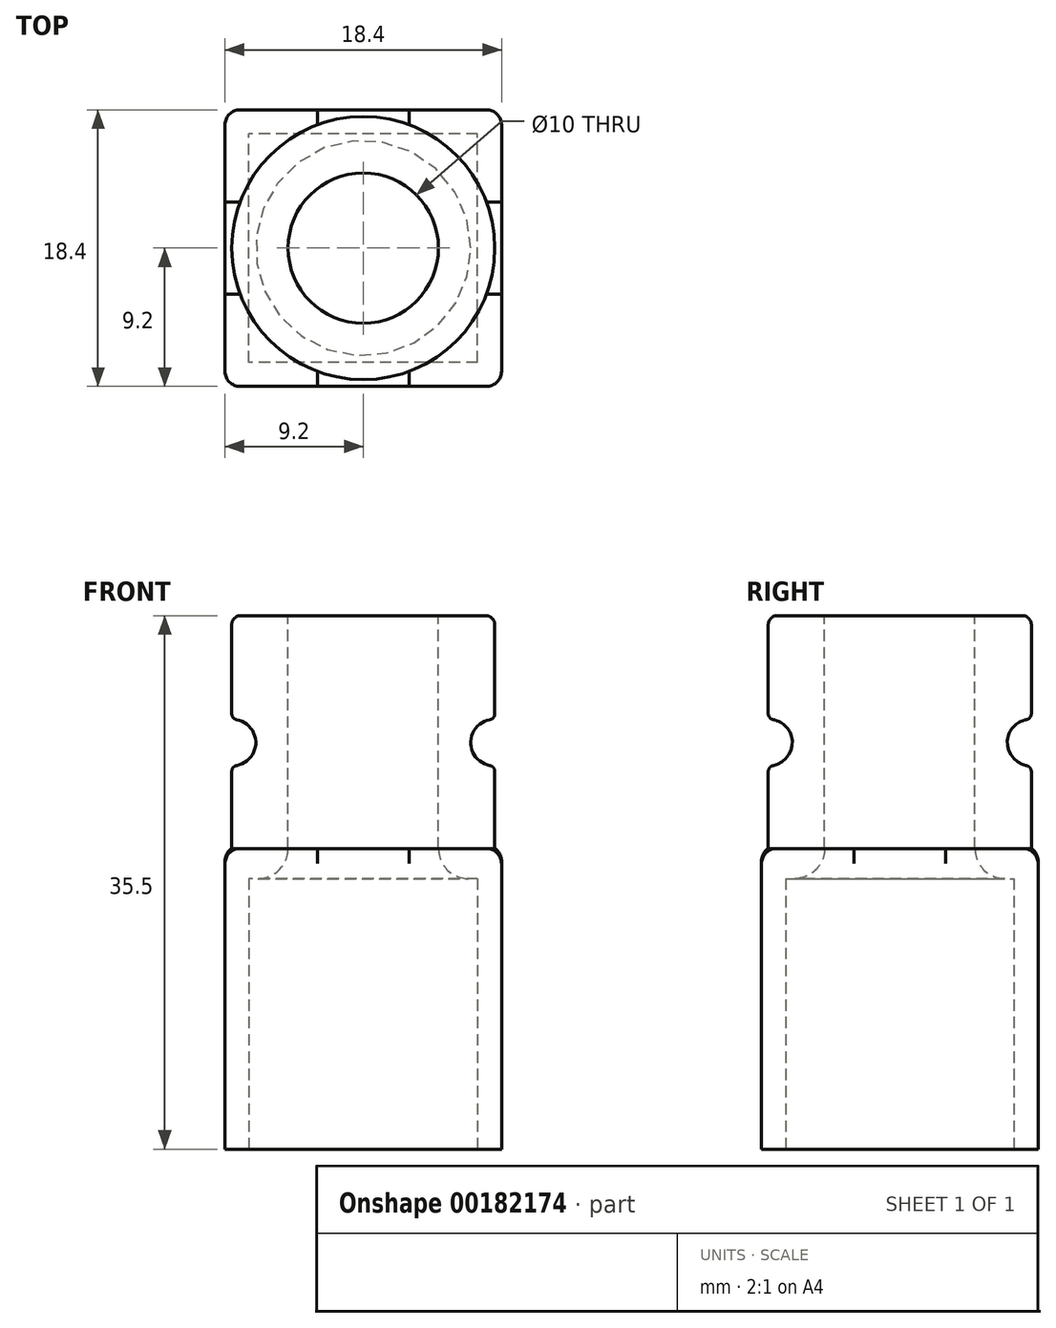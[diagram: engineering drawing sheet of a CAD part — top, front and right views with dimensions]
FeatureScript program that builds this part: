
annotation { "Feature Type Name" : "Feature", "Feature Type Description" : "" }
export const myFeature = defineFeature(function(context is Context, id is Id, definition is map)
    precondition{}
    {
        {
            var Q0;
            Q0=qCreatedBy(makeId("Top.planeOp"),FACE);
            var sketch = newSketch(context, id + "F0", { "sketchPlane" : qUnion([Q0])});
            skCircle(sketch, "E0", {"center": v(0, 0) * mm, "radius": 8.75 * mm});
            skSolve(sketch);
        }
        {
            var Q0;
            Q0 = qSketchRegion(id + "F0", true);
            extrude(context, id + "F1", {"entities" : qUnion([Q0]), "depth" : 15.5 * mm});
        }
        {
            var Q0;
            Q0=makeQuery(id+"F1.opExtrude","CAP_FACE",FACE,{"disambiguationData":[OSD([sQuery(id+"F0.wireOp",EDGE,"E0")])],"isStart":false});
            var sketch = newSketch(context, id + "F2", { "sketchPlane" : qUnion([Q0])});
            skCircle(sketch, "E1", {"center": v(0, 0) * mm, "radius": 12.72 * mm});
            skCircle(sketch, "E2", {"center": v(0, 0) * mm, "radius": 7.15 * mm});
            skSolve(sketch);
        }
        {
            var Q0;
            Q0 = qSketchRegion(id + "F2", true);
            extrude(context, id + "F3", {"entities" : qUnion([Q0]), "operationType" : NewBodyOperationType.REMOVE, "oppositeDirection" : true, "depth" : 10 * mm, "hasSecondDirection" : true, "secondDirectionOppositeDirection" : true, "secondDirectionDepth" : 6.9 * mm});
        }
        {
            var Q0;
            Q0=makeQuery(id+"F1.opExtrude","CAP_FACE",FACE,{"disambiguationData":[OSD([sQuery(id+"F0.wireOp",EDGE,"E0")])],"isStart":true});
            var sketch = newSketch(context, id + "F4", { "sketchPlane" : qUnion([Q0])});
            skLineSegment(sketch, "E3.bottom", {"start": v(9.2, 9.2) * mm, "end": v(-9.2, 9.2) * mm});
            skLineSegment(sketch, "E3.top", {"start": v(9.2, -9.2) * mm, "end": v(-9.2, -9.2) * mm});
            skLineSegment(sketch, "E3.left", {"start": v(9.2, 9.2) * mm, "end": v(9.2, -9.2) * mm});
            skLineSegment(sketch, "E3.right", {"start": v(-9.2, 9.2) * mm, "end": v(-9.2, -9.2) * mm});
            skPoint(sketch, "E3.middle", {"position": v(0, 0) * mm});
            skSolve(sketch);
        }
        {
            var Q0;
            Q0 = qSketchRegion(id + "F4", true);
            extrude(context, id + "F5", {"entities" : qUnion([Q0]), "operationType" : NewBodyOperationType.ADD, "depth" : 20 * mm});
        }
        {
            var Q0;
            Q0=makeQuery(id+"F5.opExtrude","CAP_FACE",FACE,{"disambiguationData":[OSD([sQuery(id+"F4.wireOp",EDGE,"E3.bottom"),sQuery(id+"F4.wireOp",EDGE,"E3.top"),sQuery(id+"F4.wireOp",EDGE,"E3.left"),sQuery(id+"F4.wireOp",EDGE,"E3.right")])],"isStart":false});
            var sketch = newSketch(context, id + "F6", { "sketchPlane" : qUnion([Q0])});
            skLineSegment(sketch, "E4.bottom", {"start": v(7.6, 7.6) * mm, "end": v(-7.6, 7.6) * mm});
            skLineSegment(sketch, "E4.top", {"start": v(7.6, -7.6) * mm, "end": v(-7.6, -7.6) * mm});
            skLineSegment(sketch, "E4.left", {"start": v(7.6, 7.6) * mm, "end": v(7.6, -7.6) * mm});
            skLineSegment(sketch, "E4.right", {"start": v(-7.6, 7.6) * mm, "end": v(-7.6, -7.6) * mm});
            skPoint(sketch, "E4.middle", {"position": v(0, 0) * mm});
            skSolve(sketch);
        }
        {
            var Q0;
            Q0 = qSketchRegion(id + "F6", true);
            extrude(context, id + "F7", {"entities" : qUnion([Q0]), "operationType" : NewBodyOperationType.REMOVE, "oppositeDirection" : true, "depth" : 18 * mm});
        }
        {
            var Q0;
            Q0=makeQuery(id+"F1.opExtrude","CAP_EDGE",EDGE,{"disambiguationData":[OSD([sQuery(id+"F0.wireOp",EDGE,"E0")])],"isStart":false});
            fillet(context, id + "F8", {"entities" : qUnion([Q0]), "radius" : 0.6 * mm, "tangentPropagation" : true, "allowEdgeOverflow" : false});
        }
        {
            var Q0;
            Q0=makeQuery(id+"F3.boolean.opBoolean","COPY",EDGE,{"derivedFrom":makeQuery(id+"F3.opExtrude","CAP_EDGE",EDGE,{"disambiguationData":[OSD([sQuery(id+"F2.wireOp",EDGE,"E2")])],"isStart":false})});
            var Q1;
            Q1=makeQuery(id+"F3.boolean.opBoolean","COPY",EDGE,{"derivedFrom":makeQuery(id+"F3.opExtrude","CAP_EDGE",EDGE,{"disambiguationData":[OSD([sQuery(id+"F2.wireOp",EDGE,"E2")])],"isStart":true})});
            fillet(context, id + "F9", {"entities" : qUnion([Q0, Q1]), "radius" : 1.55 * mm, "tangentPropagation" : true, "allowEdgeOverflow" : false});
        }
        {
            var Q0;
            Q0=makeQuery(id+"F5.opExtrude","SWEPT_EDGE",EDGE,{"disambiguationData":[OSD([sQuery(id+"F4.wireOp",EDGE,"E3.bottom"),sQuery(id+"F4.wireOp",EDGE,"E3.left")])]});
            var Q1;
            Q1=makeQuery(id+"F5.opExtrude","SWEPT_EDGE",EDGE,{"disambiguationData":[OSD([sQuery(id+"F4.wireOp",EDGE,"E3.top"),sQuery(id+"F4.wireOp",EDGE,"E3.left")])]});
            var Q2;
            Q2=makeQuery(id+"F5.opExtrude","SWEPT_EDGE",EDGE,{"disambiguationData":[OSD([sQuery(id+"F4.wireOp",EDGE,"E3.top"),sQuery(id+"F4.wireOp",EDGE,"E3.right")])]});
            var Q3;
            Q3=makeQuery(id+"F5.opExtrude","SWEPT_EDGE",EDGE,{"disambiguationData":[OSD([sQuery(id+"F4.wireOp",EDGE,"E3.bottom"),sQuery(id+"F4.wireOp",EDGE,"E3.right")])]});
            fillet(context, id + "F10", {"entities" : qUnion([Q0, Q1, Q2, Q3]), "radius" : 1 * mm, "tangentPropagation" : true, "allowEdgeOverflow" : false});
        }
        {
            var Q0;
            Q0=makeQuery(id+"F1.opExtrude","CAP_FACE",FACE,{"disambiguationData":[OSD([sQuery(id+"F0.wireOp",EDGE,"E0")])],"isStart":false});
            var sketch = newSketch(context, id + "F11", { "sketchPlane" : qUnion([Q0])});
            skCircle(sketch, "E5", {"center": v(0, 0) * mm, "radius": 5 * mm});
            skSolve(sketch);
        }
        {
            var Q0;
            Q0 = qSketchRegion(id + "F11", true);
            extrude(context, id + "F12", {"entities" : qUnion([Q0]), "operationType" : NewBodyOperationType.REMOVE, "oppositeDirection" : true, "depth" : 25 * mm});
        }
        {
            var Q0;
            Q0=makeQuery(id+"F12.boolean.opBoolean","INTERSECT",EDGE,{"derivedFrom":[makeQuery(id+"F7.boolean.opBoolean","COPY",FACE,{"derivedFrom":makeQuery(id+"F7.opExtrude","CAP_FACE",FACE,{"disambiguationData":[OSD([sQuery(id+"F6.wireOp",EDGE,"E4.bottom"),sQuery(id+"F6.wireOp",EDGE,"E4.top"),sQuery(id+"F6.wireOp",EDGE,"E4.left"),sQuery(id+"F6.wireOp",EDGE,"E4.right")])],"isStart":false})}),makeQuery(id+"F12.opExtrude","SWEPT_FACE",FACE,{"disambiguationData":[OSD([sQuery(id+"F11.wireOp",EDGE,"E5")])]})]});
            fillet(context, id + "F13", {"entities" : qUnion([Q0]), "radius" : 2 * mm, "tangentPropagation" : true, "allowEdgeOverflow" : false});
        }
        {
            var Q0;
            Q0=makeQuery(id+"F5.opExtrude","CAP_EDGE",EDGE,{"disambiguationData":[OSD([sQuery(id+"F4.wireOp",EDGE,"E3.bottom")])],"isStart":true});
            fillet(context, id + "F14", {"entities" : qUnion([Q0]), "radius" : 1 * mm, "tangentPropagation" : true, "allowEdgeOverflow" : false});
        }
        {
            var Q0;
            Q0=makeQuery(id+"F3.boolean.opBoolean","INTERSECT",EDGE,{"derivedFrom":[makeQuery(id+"F1.opExtrude","SWEPT_FACE",FACE,{"disambiguationData":[OSD([sQuery(id+"F0.wireOp",EDGE,"E0")])]}),makeQuery(id+"F3.opExtrude","CAP_FACE",FACE,{"disambiguationData":[OSD([sQuery(id+"F2.wireOp",EDGE,"E1"),sQuery(id+"F2.wireOp",EDGE,"E2")])],"isStart":true})]});
            var Q1;
            Q1=makeQuery(id+"F3.boolean.opBoolean","INTERSECT",EDGE,{"derivedFrom":[makeQuery(id+"F1.opExtrude","SWEPT_FACE",FACE,{"disambiguationData":[OSD([sQuery(id+"F0.wireOp",EDGE,"E0")])]}),makeQuery(id+"F3.opExtrude","CAP_FACE",FACE,{"disambiguationData":[OSD([sQuery(id+"F2.wireOp",EDGE,"E1"),sQuery(id+"F2.wireOp",EDGE,"E2")])],"isStart":false})]});
            fillet(context, id + "F15", {"entities" : qUnion([Q0, Q1]), "radius" : 0.4 * mm, "tangentPropagation" : true, "allowEdgeOverflow" : false});
        }
    });
